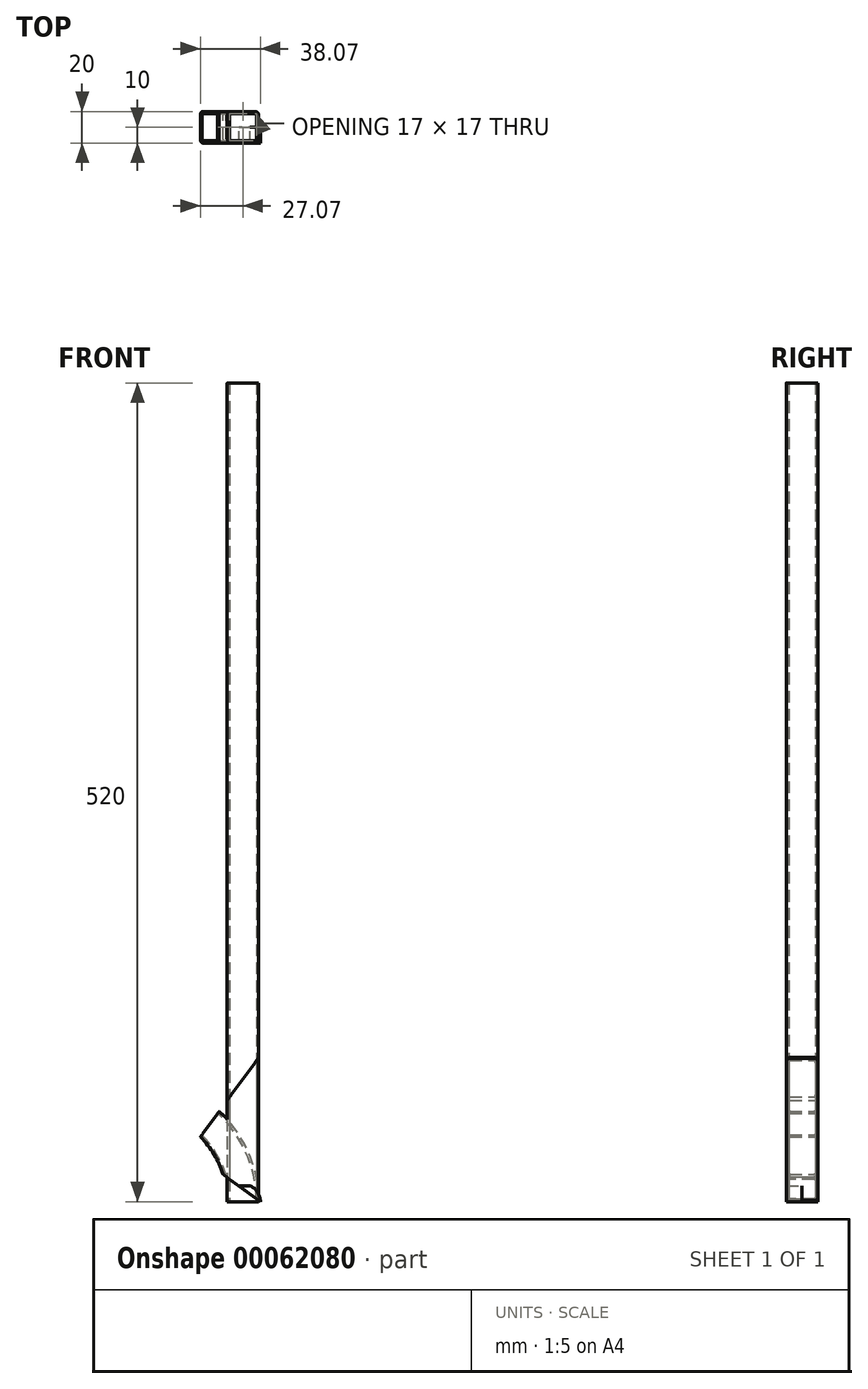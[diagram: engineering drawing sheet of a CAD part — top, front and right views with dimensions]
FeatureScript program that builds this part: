
annotation { "Feature Type Name" : "Feature", "Feature Type Description" : "" }
export const myFeature = defineFeature(function(context is Context, id is Id, definition is map)
    precondition{}
    {
        {
            assignVariable(context, id + "F0", {"name" : "w", "anyValue" : 760});
        }
        {
            assignVariable(context, id + "F1", {"name" : "l", "anyValue" : 1200});
        }
        {
            assignVariable(context, id + "F2", {"name" : "h", "anyValue" : 140});
        }
        {
            assignVariable(context, id + "F3", {"name" : "ri", "anyValue" : 58});
        }
        {
            var Q0;
            Q0=qCreatedBy(makeId("Top.planeOp"),FACE);
            var sketch = newSketch(context, id + "F4", { "sketchPlane" : qUnion([Q0])});
            skLineSegment(sketch, "E0.bottom", {"start": v(-7.5, 10) * mm, "end": v(7.5, 10) * mm});
            skLineSegment(sketch, "E0.top", {"start": v(-7.5, -10) * mm, "end": v(7.5, -10) * mm});
            skLineSegment(sketch, "E0.left", {"start": v(-10, 7.5) * mm, "end": v(-10, -7.5) * mm});
            skLineSegment(sketch, "E0.right", {"start": v(10, 7.5) * mm, "end": v(10, -7.5) * mm});
            skLineSegment(sketch, "E1", {"start": v(-10, 0) * mm, "end": v(10, 0) * mm, "construction": true});
            skPoint(sketch, "E2.visualSharp", {"position": v(-10, -10) * mm});
            skArc(sketch, "E2.filletArc", {"start": v(-10, -7.5) * mm, "mid": v(-9.27, -9.27) * mm, "end": v(-7.5, -10) * mm});
            skPoint(sketch, "E3.visualSharp", {"position": v(-10, 10) * mm});
            skArc(sketch, "E3.filletArc", {"start": v(-7.5, 10) * mm, "mid": v(-9.27, 9.27) * mm, "end": v(-10, 7.5) * mm});
            skPoint(sketch, "E4.visualSharp", {"position": v(10, 10) * mm});
            skArc(sketch, "E4.filletArc", {"start": v(10, 7.5) * mm, "mid": v(9.27, 9.27) * mm, "end": v(7.5, 10) * mm});
            skPoint(sketch, "E5.visualSharp", {"position": v(10, -10) * mm});
            skArc(sketch, "E5.filletArc", {"start": v(7.5, -10) * mm, "mid": v(9.27, -9.27) * mm, "end": v(10, -7.5) * mm});
            skLineSegment(sketch, "E6.0", {"start": v(-8.5, 7.5) * mm, "end": v(-8.5, -7.5) * mm});
            skLineSegment(sketch, "E6.1", {"start": v(-7.5, 8.5) * mm, "end": v(7.5, 8.5) * mm});
            skLineSegment(sketch, "E6.2", {"start": v(8.5, 7.5) * mm, "end": v(8.5, -7.5) * mm});
            skLineSegment(sketch, "E6.3", {"start": v(-7.5, -8.5) * mm, "end": v(7.5, -8.5) * mm});
            skPoint(sketch, "E7.visualSharp", {"position": v(-8.5, 8.5) * mm});
            skArc(sketch, "E7.filletArc", {"start": v(-7.5, 8.5) * mm, "mid": v(-8.2, 8.2) * mm, "end": v(-8.5, 7.5) * mm});
            skPoint(sketch, "E8.visualSharp", {"position": v(8.5, 8.5) * mm});
            skArc(sketch, "E8.filletArc", {"start": v(8.5, 7.5) * mm, "mid": v(8.2, 8.2) * mm, "end": v(7.5, 8.5) * mm});
            skPoint(sketch, "E9.visualSharp", {"position": v(8.5, -8.5) * mm});
            skArc(sketch, "E9.filletArc", {"start": v(7.5, -8.5) * mm, "mid": v(8.2, -8.2) * mm, "end": v(8.5, -7.5) * mm});
            skPoint(sketch, "E10.visualSharp", {"position": v(-8.5, -8.5) * mm});
            skArc(sketch, "E10.filletArc", {"start": v(-8.5, -7.5) * mm, "mid": v(-8.2, -8.2) * mm, "end": v(-7.5, -8.5) * mm});
            skLineSegment(sketch, "E11", {"start": v(-68, 7.5) * mm, "end": v(-68, -7.5) * mm});
            skLineSegment(sketch, "E12", {"start": v(-68, 0) * mm, "end": v(-10, 0) * mm, "construction": true});
            skSolve(sketch);
        }
        {
            var Q0;
            Q0 = qSketchRegion(id + "F4", true);
            extrude(context, id + "F5", {"entities" : qUnion([Q0]), "endBound" : BoundingType.SYMMETRIC, "depth" : ((getVariable(context, 'w')) - 40) * mm});
        }
        {
            var Q0;
            Q0 = qSketchRegion(id + "F4", true);
            extrude(context, id + "F6", {"entities" : qUnion([Q0]), "depth" : ((getVariable(context, 'h')) - 40) * mm});
        }
        {
            var Q0;
            Q0 = qSketchRegion(id + "F4", true);
            extrude(context, id + "F7", {"entities" : qUnion([Q0]), "oppositeDirection" : true, "depth" : ((getVariable(context, 'w')) - 40 - ((getVariable(context, 'ri')) * 2)) * mm});
        }
        {
            var Q0;
            Q0=makeQuery(id+"F4.imprint","IMPRINT",FACE,{"disambiguationData":[TD([[makeQuery(id+"F4.imprint","IMPRINT",EDGE,{"derivedFrom":sQuery(id+"F4.wireOp",EDGE,"E0.bottom")}),-1.0]])]});
            extrude(context, id + "F8", {"entities" : qUnion([Q0]), "depth" : ((getVariable(context, 'l')) - 40 - ((getVariable(context, 'ri')) * 2)) * mm});
        }
        {
            var Q0;
            Q0=makeQuery(id+"F4.imprint","IMPRINT",FACE,{"disambiguationData":[TD([[makeQuery(id+"F4.imprint","IMPRINT",EDGE,{"derivedFrom":sQuery(id+"F4.wireOp",EDGE,"E0.bottom")}),-1.0]])]});
            var Q1;
            Q1=sQuery(id+"F4.wireOp",EDGE,"E11");
            revolve(context, id + "F9", {"entities" : qUnion([Q0]), "axis" : qUnion([Q1]), "revolveType" : RevolveType.ONE_DIRECTION, "angle" : 90 * degree});
        }
        {
            var Q0;
            Q0=qCreatedBy(makeId("Front.planeOp"),FACE);
            var sketch = newSketch(context, id + "F10", { "sketchPlane" : qUnion([Q0])});
            skCircle(sketch, "E13", {"center": v(0, 0) * mm, "radius": 10 * mm});
            skCircle(sketch, "E14", {"center": v(0, 0) * mm, "radius": 5 * mm});
            skCircle(sketch, "E15", {"center": v(0, 0) * mm, "radius": 11 * mm});
            skLineSegment(sketch, "E16", {"start": v(-10, 4.58) * mm, "end": v(-10, -4.58) * mm});
            skLineSegment(sketch, "E17", {"start": v(-4.58, 10) * mm, "end": v(4.58, 10) * mm});
            skSolve(sketch);
        }
        {
            var Q0;
            Q0=makeQuery(id+"F10.imprint","IMPRINT",FACE,{"disambiguationData":[TD([[makeQuery(id+"F10.imprint","IMPRINT",EDGE,{"derivedFrom":sQuery(id+"F10.wireOp",EDGE,"E13")}),1.0]])]});
            var Q1;
            {var subQ0=sQuery(id+"F10.wireOp",EDGE,"E16");var subQ1=sQuery(id+"F10.wireOp",EDGE,"E13");var subQ2=makeQuery(id+"F10.imprint","INTERSECT",VERTEX,{"derivedFrom":[subQ1,subQ0]});Q1=makeQuery(id+"F10.imprint","IMPRINT",FACE,{"disambiguationData":[TD([[makeQuery(id+"F10.imprint","IMPRINT",EDGE,{"disambiguationData":[TD([[subQ2,1.0]])],"derivedFrom":subQ1}),-1.0]])]});}
            var Q2;
            {var subQ0=sQuery(id+"F10.wireOp",EDGE,"E16");var subQ1=sQuery(id+"F10.wireOp",EDGE,"E13");var subQ2=makeQuery(id+"F10.imprint","INTERSECT",VERTEX,{"derivedFrom":[subQ1,subQ0]});Q2=makeQuery(id+"F10.imprint","IMPRINT",FACE,{"disambiguationData":[TD([[makeQuery(id+"F10.imprint","IMPRINT",EDGE,{"disambiguationData":[TD([[subQ2,-1.0]])],"derivedFrom":subQ1}),-1.0]])]});}
            extrude(context, id + "F11", {"entities" : qUnion([Q0, Q1, Q2]), "depth" : 20 * mm});
        }
        {
            var Q0;
            Q0 = qSketchRegion(id + "F4", true);
            extrude(context, id + "F12", {"entities" : qUnion([Q0]), "depth" : 111 * mm});
        }
        {
            var Q0;
            Q0 = qSketchRegion(id + "F4", true);
            extrude(context, id + "F13", {"entities" : qUnion([Q0]), "depth" : 91 * mm});
        }
        {
            var Q0;
            Q0 = qSketchRegion(id + "F4", true);
            extrude(context, id + "F14", {"entities" : qUnion([Q0]), "depth" : 120 * mm});
        }
        {
            var Q0;
            Q0=makeQuery(id+"F14.opExtrude","SWEPT_FACE",FACE,{"disambiguationData":[OSD([sQuery(id+"F4.wireOp",EDGE,"E0.top")])]});
            var sketch = newSketch(context, id + "F15", { "sketchPlane" : qUnion([Q0])});
            skLineSegment(sketch, "E18", {"start": v(-33.35, 32.53) * mm, "end": v(11, 93) * mm});
            skLineSegment(sketch, "E19", {"start": v(11, 93) * mm, "end": v(11, 0) * mm});
            skLineSegment(sketch, "E20", {"start": v(11, 0) * mm, "end": v(-33.35, 32.53) * mm});
            skLineSegment(sketch, "E21", {"start": v(0, 0) * mm, "end": v(11, 0) * mm, "construction": true});
            skSolve(sketch);
        }
        {
            var Q0;
            {var subQ0=sQuery(id+"F15.wireOp",EDGE,"E20");var subQ1=sQuery(id+"F15.wireOp",EDGE,"E18");var subQ2=makeQuery(id+"F15.imprint","INTERSECT",VERTEX,{"derivedFrom":[subQ1,subQ0]});Q0=makeQuery(id+"F15.imprint","IMPRINT",FACE,{"disambiguationData":[TD([[makeQuery(id+"F15.imprint","IMPRINT",EDGE,{"disambiguationData":[TD([[subQ2,-1.0]])],"derivedFrom":subQ1}),-1.0]])]});}
            var Q1;
            {var subQ0=sQuery(id+"F15.wireOp",EDGE,"E18");var subQ1=sQuery(id+"F4.wireOp",EDGE,"E0.top");var subQ2=makeQuery(id+"F14.opExtrude","SWEPT_EDGE",EDGE,{"disambiguationData":[OSD([subQ1,sQuery(id+"F4.wireOp",EDGE,"E2.filletArc")])]});var subQ3=makeQuery(id+"F15.imprint","INTERSECT",VERTEX,{"derivedFrom":[subQ2,subQ0]});Q1=makeQuery(id+"F15.imprint","IMPRINT",FACE,{"disambiguationData":[TD([[makeQuery(id+"F15.imprint","IMPRINT",EDGE,{"disambiguationData":[TD([[subQ3,-1.0]])],"derivedFrom":subQ0}),-1.0]])]});}
            var Q2;
            {var subQ0=sQuery(id+"F15.wireOp",EDGE,"E19");Q2=makeQuery(id+"F15.imprint","IMPRINT",FACE,{"disambiguationData":[TD([[makeQuery(id+"F15.imprint","IMPRINT",EDGE,{"derivedFrom":subQ0}),-1.0]])]});}
            extrude(context, id + "F16", {"entities" : qUnion([Q0, Q1, Q2]), "operationType" : NewBodyOperationType.INTERSECT, "oppositeDirection" : true, "depth" : 25 * mm});
        }
        {
            var Q0;
            Q0 = qSketchRegion(id + "F4", true);
            extrude(context, id + "F17", {"entities" : qUnion([Q0]), "depth" : 520 * mm});
        }
    });
